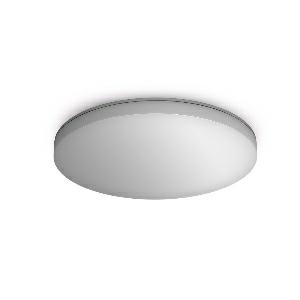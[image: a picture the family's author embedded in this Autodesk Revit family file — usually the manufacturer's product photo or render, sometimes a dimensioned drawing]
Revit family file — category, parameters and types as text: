
# Revit family: rs_pro_connect_r20_sl_057084
name_source: partatom
category: Leuchten
revit_build: Autodesk Revit 2016 (Build: 20190508_0715(x64)
units: mm (PartAtom-declared; Revit-internal decimal feet)

## family parameters
Basisbauteil = Fläche
Beim Laden mit Abzugskörper schneiden = Nein
Bemaßung runder Anschluss = Durchmesser verwenden
Gemeinsam genutzt = Nein
Lichtquelle = Nein
Raumberechnungspunkt = Nein
Teiletyp = Normal

## types (1)
- RS PRO Connect R20 SL (1 x , 2000 lm, 4000 K)
    Beschreibung = Dimensions (Ø x H): 350 x 55 mm; Mains power supply: 220 – 240 V / 50 – 60 Hz; Output: 16 W; Luminous flux: 2000 lm; Colour temperature: 4000 K; Colour variation LED: SDCM3; Colour Rendering Index CRI: 80-89; With lamp: Yes, STEINEL LED system; Lamp: LED cannot be replaced; LED life expectancy (max. °C): 50000 h; LED life expectancy (25 °C): 60000 h; Drop in luminous flux in accordance with LM80: L80B50; Base: without; LED cooling system: Passive Thermo Control; With motion detector: No; Main light adjustable: 50 - 100 %; Continuous light: selectable; Photo-cell controller: No; Basic light level function, detail: LED Backlight; Functions: Backlight; Soft light start: Yes; Impact resistance: IK07; IP-rating: IP40; Protection class: II; Ambient temperature: -20 – 40 °C; Housing material: Plastic; Cover material: PC, opal; Manufacturer's Warranty: 5 years; Settings via: Bluetooth; With remote control: No; Version: Neutral white; PU1, EAN: 4007841057084
    CIE Flux Codes = 45 76 94 94 100
    Color Rendering = 80-89
    Color Temperature = 4000 K
    Frequency = 50 Hz, 60 Hz
    Height = 0 mm  [stored 0 ft]
    Hersteller = Steinel
    Lamp Light Flux = 2000 lm
    Lamp count = 1
    Lampe = 1 x
    Length = 350 mm
    Luminous efficacy = 0 lm/W
    ModVariant = Nein
    Modell = 057084
    Mounting Type = Surface mounted
    Number of Poles = 1
    OnlyDefault = Ja
    Power Factor = 1
    Product Name = RS PRO Connect R20 SL
    Product group = Sensor-switched indoor light
    ProductGroupID = 30
    Protection Class = Protection class II
    Protection Degree = IP 40
    RlxData = <blob elided: 175185 chars, md5=02864fbf>
    Scheinlast = 0 VA
    Socket = socket
    Standby Power = 0 W
    System Light Flux = 0 lm
    System Power = 0 W
    Typenbild = produkt1_057084.jpg
    Typenkommentare = Product without accessories
    URL = http://relux.com
    VarID = ---
    Voltage = 0 V
    Vorgabe-Ansicht = 1800 mm
    Weight = 0.00 kg
    Width = 0 mm  [stored 0 ft]

note: [stored X ft] marks values corroborated as IEEE doubles in the binary element streams (Revit-internal decimal feet)

## geometry (parser evidence)
native form markers: Sweep x16
no freeform markers — native parametric forms only
